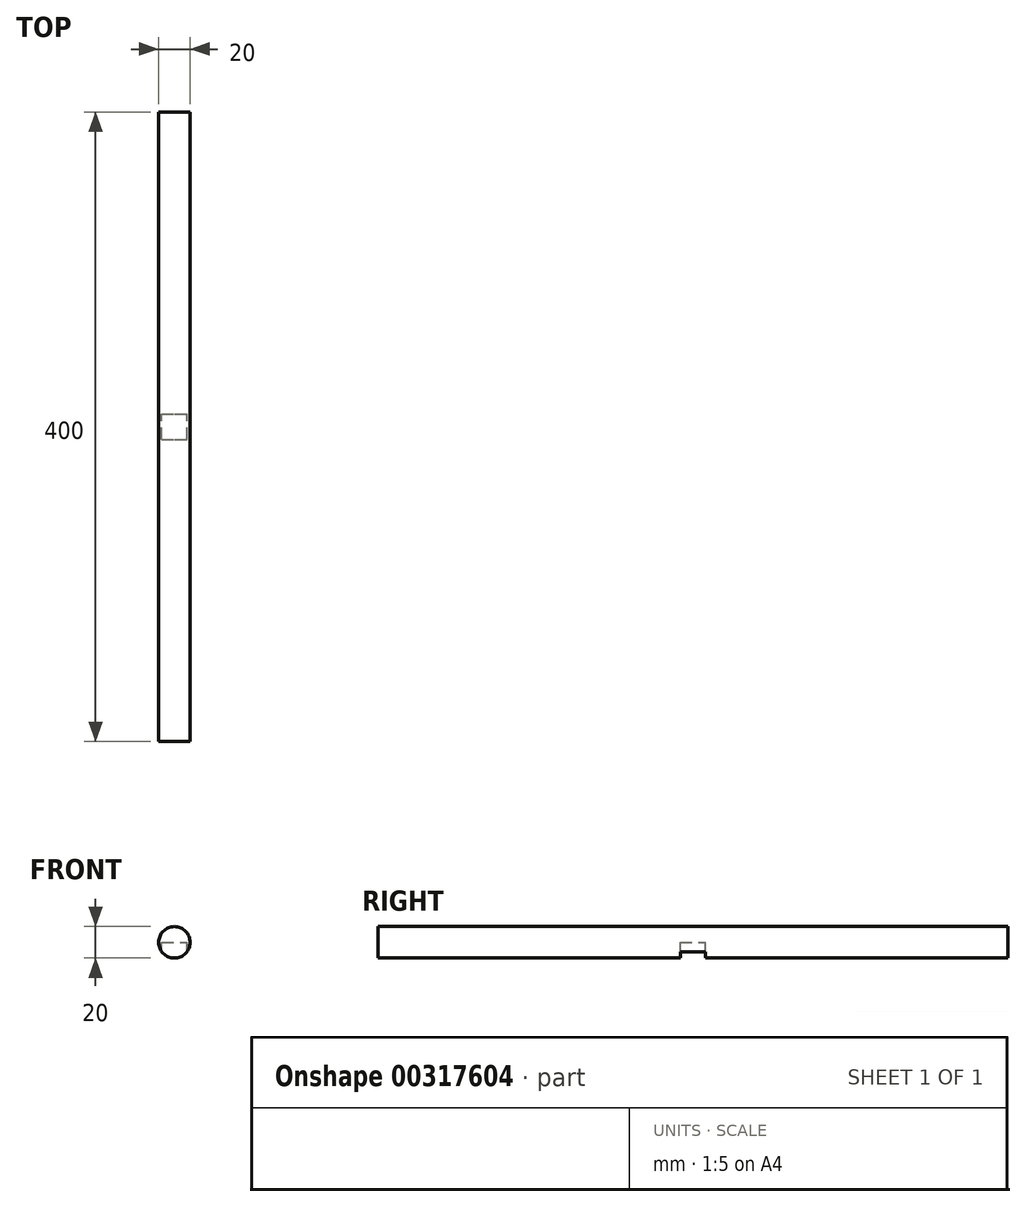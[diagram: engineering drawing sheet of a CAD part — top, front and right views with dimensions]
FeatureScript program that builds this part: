
annotation { "Feature Type Name" : "Feature", "Feature Type Description" : "" }
export const myFeature = defineFeature(function(context is Context, id is Id, definition is map)
    precondition{}
    {
        {
            var Q0;
            Q0=qCreatedBy(makeId("Front.planeOp"),FACE);
            var sketch = newSketch(context, id + "F0", { "sketchPlane" : qUnion([Q0])});
            skCircle(sketch, "E0", {"center": v(0, 0) * mm, "radius": 10 * mm});
            skSolve(sketch);
        }
        {
            var Q0;
            Q0=makeQuery(id+"F0.imprint","IMPRINT",FACE,{"disambiguationData":[TD([[makeQuery(id+"F0.imprint","IMPRINT",EDGE,{"derivedFrom":sQuery(id+"F0.wireOp",EDGE,"E0")}),1.0]])]});
            extrude(context, id + "F1", {"entities" : qUnion([Q0]), "depth" : 200 * mm, "hasSecondDirection" : true, "secondDirectionOppositeDirection" : true, "secondDirectionDepth" : 200 * mm});
        }
        {
            var Q0;
            Q0=qCreatedBy(makeId("Top.planeOp"),FACE);
            var sketch = newSketch(context, id + "F2", { "sketchPlane" : qUnion([Q0])});
            skLineSegment(sketch, "E1.bottom", {"start": v(-8, -8) * mm, "end": v(8, -8) * mm});
            skLineSegment(sketch, "E1.top", {"start": v(-8, 8) * mm, "end": v(8, 8) * mm});
            skLineSegment(sketch, "E1.left", {"start": v(-8, -8) * mm, "end": v(-8, 8) * mm});
            skLineSegment(sketch, "E1.right", {"start": v(8, -8) * mm, "end": v(8, 8) * mm});
            skSolve(sketch);
        }
        {
            var Q0;
            Q0 = qSketchRegion(id + "F2", true);
            extrude(context, id + "F3", {"entities" : qUnion([Q0]), "operationType" : NewBodyOperationType.REMOVE, "oppositeDirection" : true, "depth" : 25 * mm});
        }
    });
